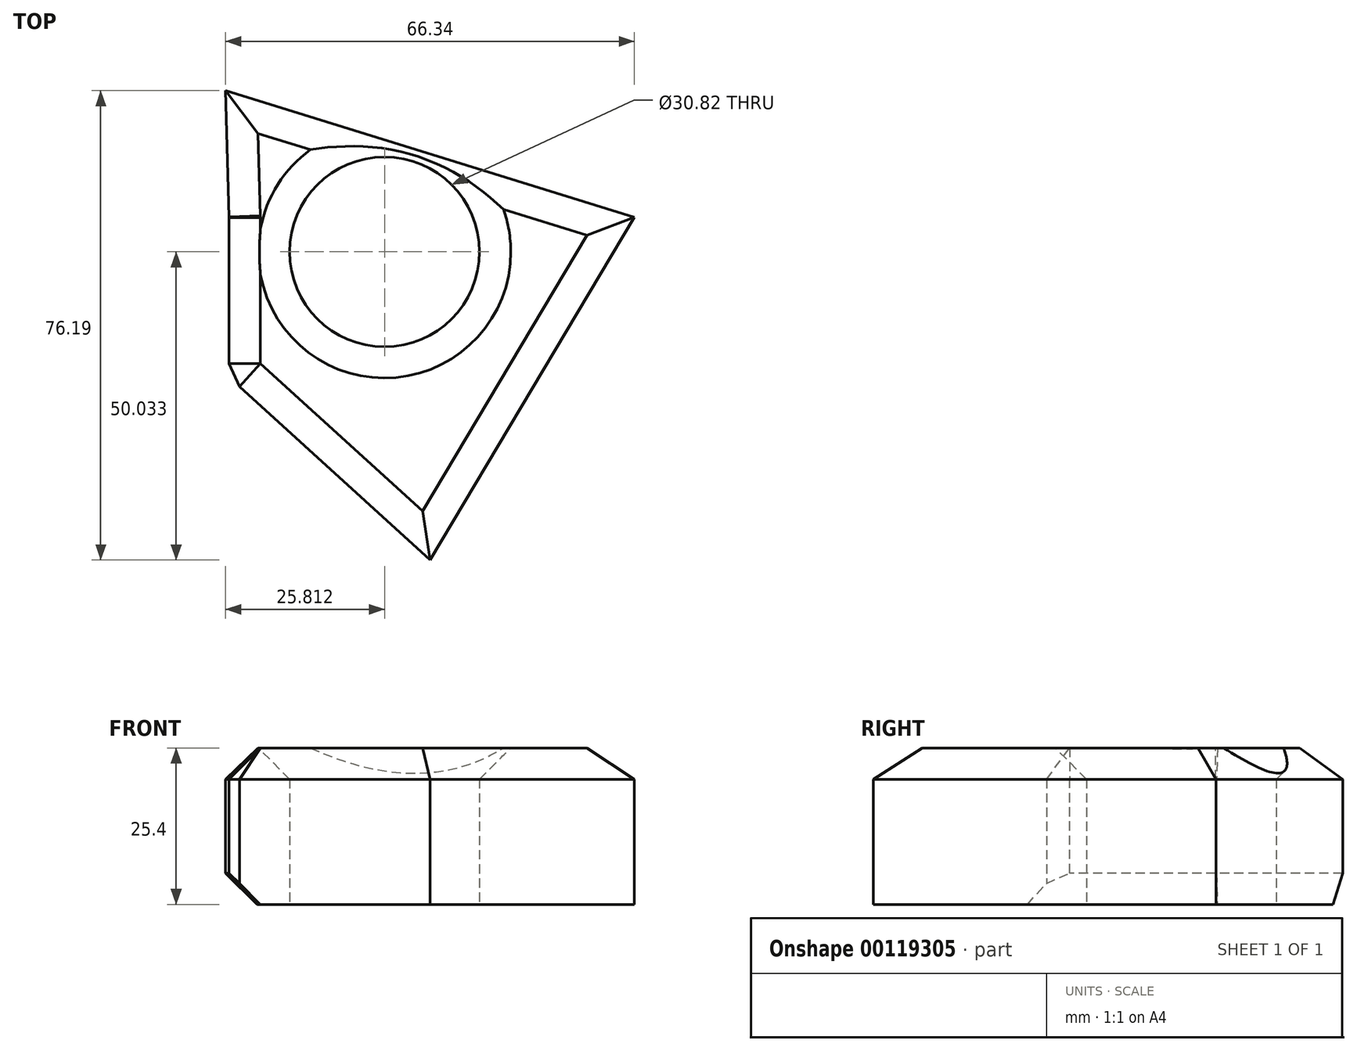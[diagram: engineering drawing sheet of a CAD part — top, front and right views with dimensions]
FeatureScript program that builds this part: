
annotation { "Feature Type Name" : "Feature", "Feature Type Description" : "" }
export const myFeature = defineFeature(function(context is Context, id is Id, definition is map)
    precondition{}
    {
        {
            var Q0;
            Q0=qCreatedBy(makeId("Top.planeOp"),FACE);
            var sketch = newSketch(context, id + "F0", { "sketchPlane" : qUnion([Q0])});
            skLineSegment(sketch, "E0", {"start": v(-32.6, 55.66) * mm, "end": v(-32.6, 29.64) * mm});
            skLineSegment(sketch, "E1", {"start": v(-32.6, 29.64) * mm, "end": v(0, 0) * mm});
            skLineSegment(sketch, "E2", {"start": v(-33.18, 76.2) * mm, "end": v(33.16, 55.66) * mm});
            skLineSegment(sketch, "E3", {"start": v(-32.6, 55.66) * mm, "end": v(-33.18, 76.2) * mm});
            skLineSegment(sketch, "E4", {"start": v(0, 0) * mm, "end": v(33.16, 55.66) * mm});
            skCircle(sketch, "E5", {"center": v(-7.37, 50.03) * mm, "radius": 15.4 * mm});
            skSolve(sketch);
        }
        {
            var Q0;
            Q0=makeQuery(id+"F0.imprint","IMPRINT",FACE,{"disambiguationData":[TD([[makeQuery(id+"F0.imprint","IMPRINT",EDGE,{"derivedFrom":sQuery(id+"F0.wireOp",EDGE,"E0")}),1.0]])]});
            extrude(context, id + "F1", {"entities" : qUnion([Q0]), "depth" : 25.4 * mm});
        }
        {
            var Q0;
            Q0=makeQuery(id+"F1.opExtrude","SWEPT_FACE",FACE,{"disambiguationData":[OSD([sQuery(id+"F0.wireOp",EDGE,"E0")])]});
            var Q1;
            Q1=makeQuery(id+"F1.opExtrude","CAP_EDGE",EDGE,{"disambiguationData":[OSD([sQuery(id+"F0.wireOp",EDGE,"E0")])],"isStart":true});
            var Q2;
            Q2=makeQuery(id+"F1.opExtrude","CAP_FACE",FACE,{"disambiguationData":[OSD([sQuery(id+"F0.wireOp",EDGE,"E0"),sQuery(id+"F0.wireOp",EDGE,"E1"),sQuery(id+"F0.wireOp",EDGE,"E2"),sQuery(id+"F0.wireOp",EDGE,"E3"),sQuery(id+"F0.wireOp",EDGE,"E4"),sQuery(id+"F0.wireOp",EDGE,"E5")])],"isStart":false});
            chamfer(context, id + "F2", {"entities" : qUnion([Q0, Q1, Q2]), "width" : 5.08 * mm, "tangentPropagation" : true});
        }
    });
